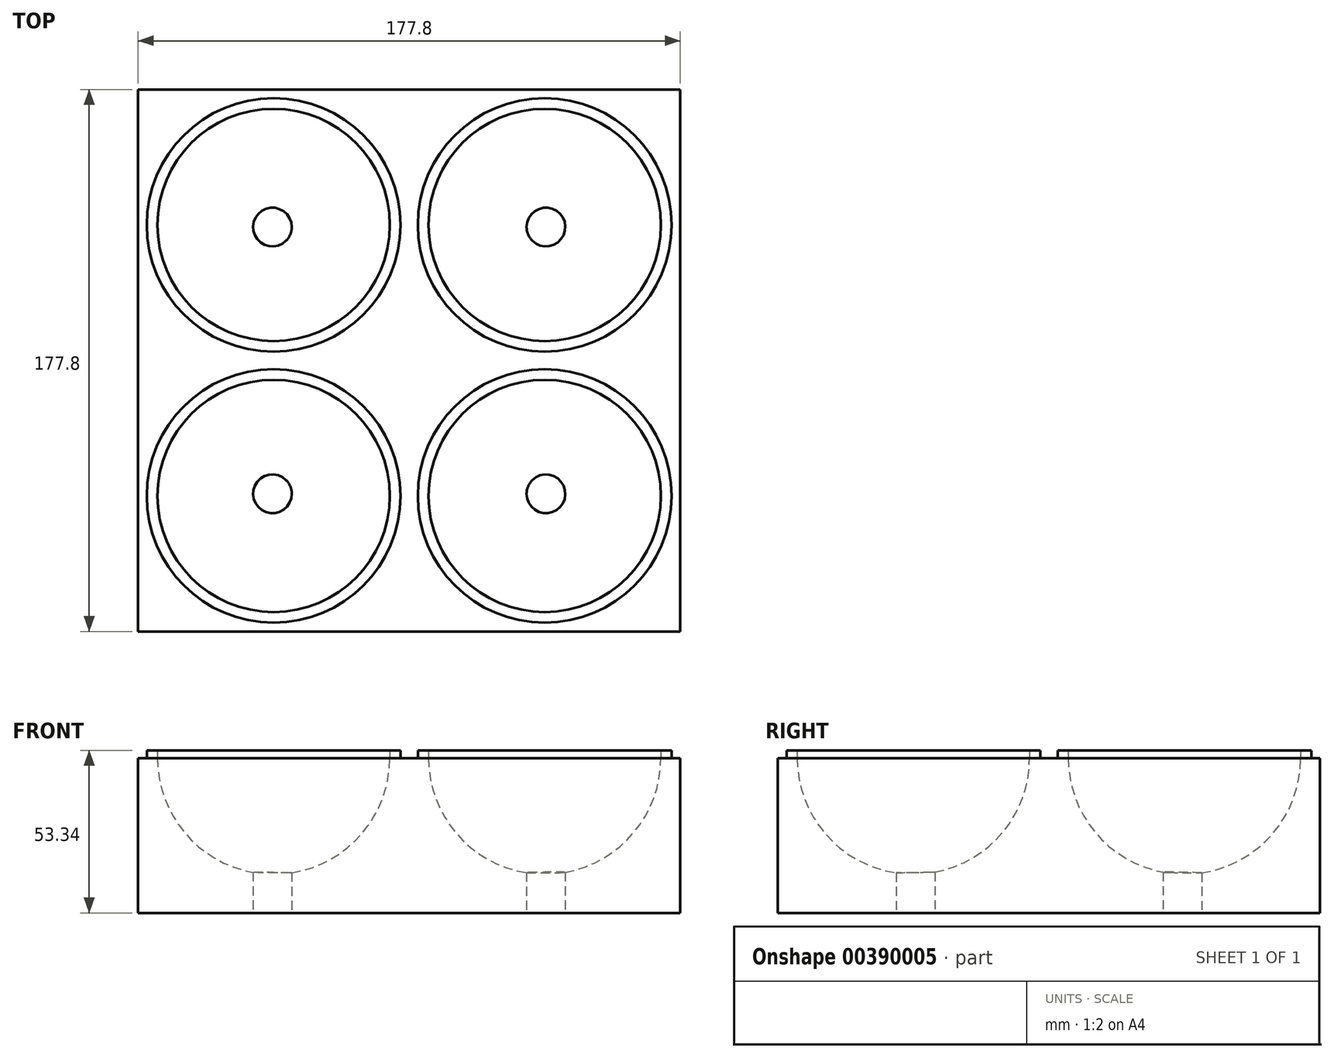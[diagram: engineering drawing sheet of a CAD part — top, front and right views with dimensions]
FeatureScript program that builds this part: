
annotation { "Feature Type Name" : "Feature", "Feature Type Description" : "" }
export const myFeature = defineFeature(function(context is Context, id is Id, definition is map)
    precondition{}
    {
        {
            var Q0;
            Q0=qCreatedBy(makeId("Top.planeOp"),FACE);
            var sketch = newSketch(context, id + "F0", { "sketchPlane" : qUnion([Q0])});
            skLineSegment(sketch, "E0.bottom", {"start": v(143.29, 0) * mm, "end": v(54.39, 0) * mm});
            skLineSegment(sketch, "E0.top", {"start": v(143.29, 88.9) * mm, "end": v(54.39, 88.9) * mm});
            skLineSegment(sketch, "E0.left", {"start": v(143.29, 0) * mm, "end": v(143.29, 88.9) * mm});
            skLineSegment(sketch, "E0.right", {"start": v(54.39, 0) * mm, "end": v(54.39, 88.9) * mm});
            skSolve(sketch);
        }
        {
            var Q0;
            Q0=qSketchRegion(id+"F0",true);
            extrude(context, id + "F1", {"entities" : qUnion([Q0]), "depth" : 50.8 * mm});
        }
        {
            var Q0;
            Q0=makeQuery(id+"F1.opExtrude","CAP_FACE",FACE,{"disambiguationData":[OSD([sQuery(id+"F0.wireOp",EDGE,"E0.bottom"),sQuery(id+"F0.wireOp",EDGE,"E0.top"),sQuery(id+"F0.wireOp",EDGE,"E0.left"),sQuery(id+"F0.wireOp",EDGE,"E0.right")])],"isStart":false});
            var sketch = newSketch(context, id + "F2", { "sketchPlane" : qUnion([Q0])});
            skLineSegment(sketch, "E1", {"start": v(143.29, 44.45) * mm, "end": v(54.39, 44.45) * mm});
            skArc(sketch, "E2", {"start": v(60.74, 44.45) * mm, "mid": v(98.84, 6.35) * mm, "end": v(136.94, 44.45) * mm});
            skLineSegment(sketch, "E3", {"start": v(60.74, 44.45) * mm, "end": v(57.44, 44.45) * mm});
            skLineSegment(sketch, "E4", {"start": v(57.44, 44.45) * mm, "end": v(60.74, 44.45) * mm});
            skSolve(sketch);
        }
        {
            var Q0;
            {var subQ0=sQuery(id+"F2.wireOp",EDGE,"E2");Q0=makeQuery(id+"F2.imprint","IMPRINT",FACE,{"disambiguationData":[TD([[makeQuery(id+"F2.imprint","IMPRINT",EDGE,{"derivedFrom":subQ0}),1.0]])]});}
            var Q1;
            Q1=sQuery(id+"F2.wireOp",EDGE,"I0gMvy8E-v0mp-4M6N-690x-ToUl01OIbrME");
            var Q2;
            Q2=sQuery(id+"F2.wireOp",EDGE,"E1");
            revolve(context, id + "F3", {"operationType" : NewBodyOperationType.REMOVE, "entities" : qUnion([Q0]), "surfaceEntities" : qUnion([Q1]), "axis" : qUnion([Q2]), "revolveType" : RevolveType.ONE_DIRECTION, "oppositeDirection" : true, "angle" : 180 * degree});
        }
        {
            var Q0;
            Q0=makeQuery(id+"F1.opExtrude","CAP_FACE",FACE,{"disambiguationData":[OSD([sQuery(id+"F0.wireOp",EDGE,"E0.bottom"),sQuery(id+"F0.wireOp",EDGE,"E0.top"),sQuery(id+"F0.wireOp",EDGE,"E0.left"),sQuery(id+"F0.wireOp",EDGE,"E0.right")])],"isStart":false});
            var sketch = newSketch(context, id + "F4", { "sketchPlane" : qUnion([Q0])});
            skCircle(sketch, "E5", {"center": v(98.84, 44.45) * mm, "radius": 41.6 * mm});
            skSolve(sketch);
        }
        {
            var Q0;
            Q0=makeQuery(id+"F4.imprint","IMPRINT",FACE,{"disambiguationData":[TD([[makeQuery(id+"F4.imprint","IMPRINT",EDGE,{"derivedFrom":sQuery(id+"F4.wireOp",EDGE,"E5")}),1.0]])]});
            extrude(context, id + "F5", {"entities" : qUnion([Q0]), "operationType" : NewBodyOperationType.ADD, "depth" : 2.54 * mm});
        }
        {
            var Q0;
            Q0=makeQuery(id+"F1.opExtrude","CAP_FACE",FACE,{"disambiguationData":[OSD([sQuery(id+"F0.wireOp",EDGE,"E0.bottom"),sQuery(id+"F0.wireOp",EDGE,"E0.top"),sQuery(id+"F0.wireOp",EDGE,"E0.left"),sQuery(id+"F0.wireOp",EDGE,"E0.right")])],"isStart":true});
            var sketch = newSketch(context, id + "F6", { "sketchPlane" : qUnion([Q0])});
            skCircle(sketch, "E6", {"center": v(99.24, -43.76) * mm, "radius": 6.35 * mm});
            skSolve(sketch);
        }
        {
            var Q0;
            Q0=makeQuery(id+"F6.imprint","IMPRINT",FACE,{"disambiguationData":[TD([[makeQuery(id+"F6.imprint","IMPRINT",EDGE,{"derivedFrom":sQuery(id+"F6.wireOp",EDGE,"E6")}),1.0]])]});
            var Q1;
            Q1=sQuery(id+"F6.wireOp",EDGE,"E6");
            extrude(context, id + "F7", {"entities" : qUnion([Q0]), "operationType" : NewBodyOperationType.REMOVE, "surfaceEntities" : qUnion([Q1]), "oppositeDirection" : true, "depth" : 25.4 * mm});
        }
        {
            var Q0;
            Q0=makeQuery(id+"F1.opExtrude","SWEPT_BODY",BODY,{"disambiguationData":[OSD([sQuery(id+"F0.wireOp",EDGE,"E0.bottom"),sQuery(id+"F0.wireOp",EDGE,"E0.top"),sQuery(id+"F0.wireOp",EDGE,"E0.left"),sQuery(id+"F0.wireOp",EDGE,"E0.right")])]});
            var Q1;
            Q1=makeQuery(id+"F1.opExtrude","SWEPT_FACE",FACE,{"disambiguationData":[OSD([sQuery(id+"F0.wireOp",EDGE,"E0.right")])]});
            mirror(context, id + "F8", {"operationType" : NewBodyOperationType.ADD, "entities" : qUnion([Q0]), "mirrorPlane" : qUnion([Q1])});
        }
        {
            var Q0;
            Q0=makeQuery(id+"F1.opExtrude","SWEPT_BODY",BODY,{"disambiguationData":[OSD([sQuery(id+"F0.wireOp",EDGE,"E0.bottom"),sQuery(id+"F0.wireOp",EDGE,"E0.top"),sQuery(id+"F0.wireOp",EDGE,"E0.left"),sQuery(id+"F0.wireOp",EDGE,"E0.right")])]});
            var Q1;
            {var subQ0=makeQuery(id+"F1.opExtrude","SWEPT_FACE",FACE,{"disambiguationData":[OSD([sQuery(id+"F0.wireOp",EDGE,"E0.bottom")])]});Q1=makeQuery(id+"F8.boolean.opBoolean","MERGE",FACE,{"derivedFrom":[subQ0,makeQuery(id+"F8.opPattern","COPY",FACE,{"derivedFrom":subQ0,"instanceName":"1"})]});}
            mirror(context, id + "F9", {"operationType" : NewBodyOperationType.ADD, "entities" : qUnion([Q0]), "mirrorPlane" : qUnion([Q1])});
        }
    });
